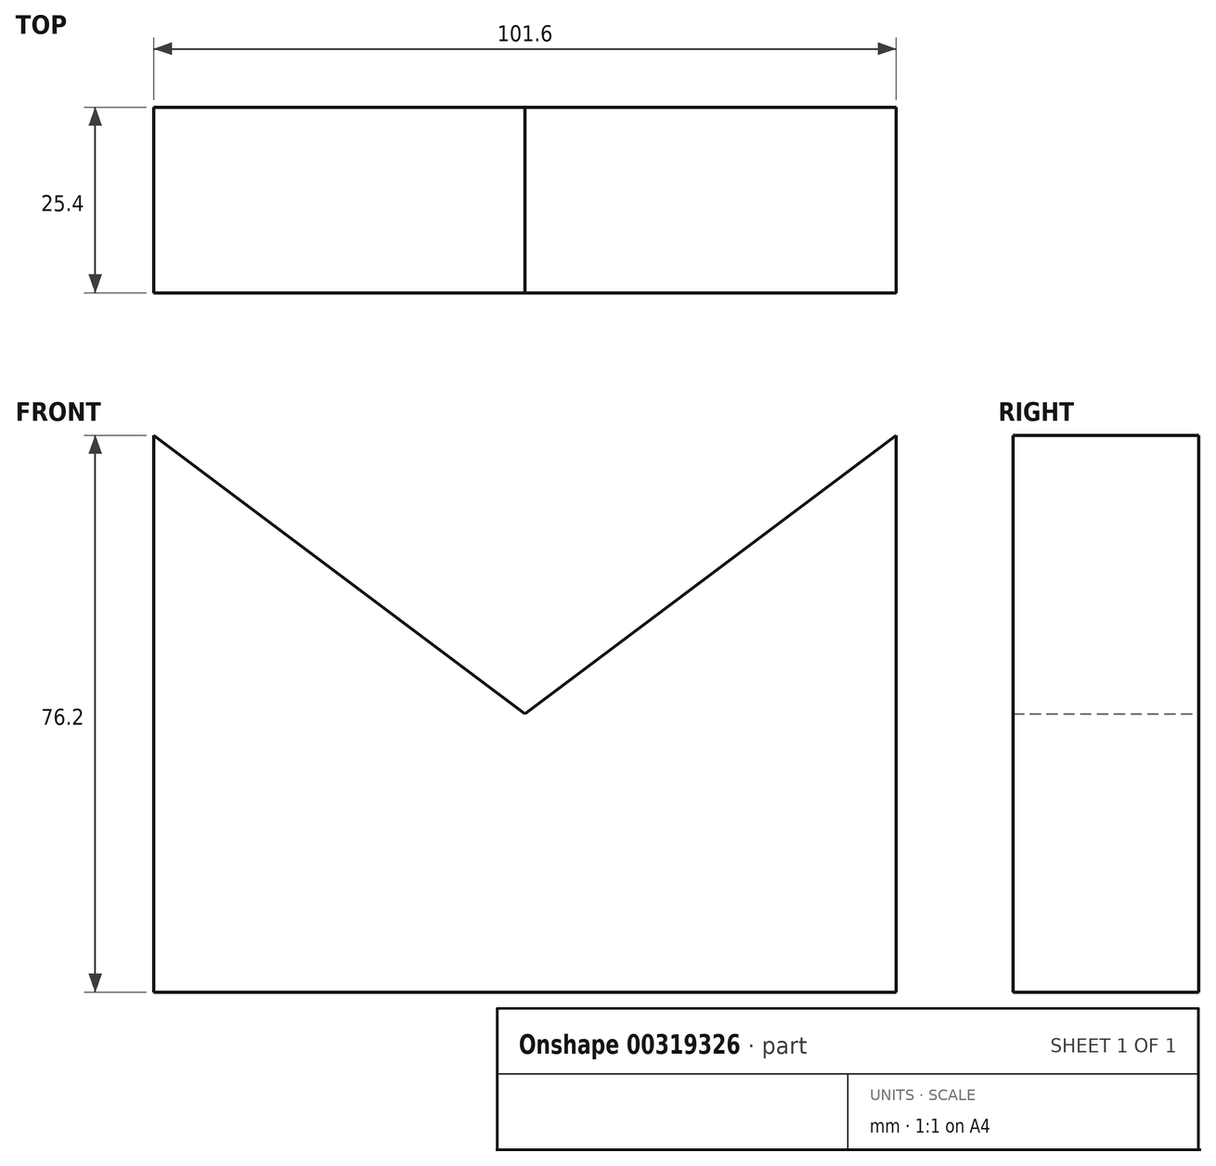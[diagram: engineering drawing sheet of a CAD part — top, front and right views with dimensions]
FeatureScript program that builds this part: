
annotation { "Feature Type Name" : "Feature", "Feature Type Description" : "" }
export const myFeature = defineFeature(function(context is Context, id is Id, definition is map)
    precondition{}
    {
        {
            var Q0;
            Q0=qCreatedBy(makeId("Front.planeOp"),FACE);
            var sketch = newSketch(context, id + "F0", { "sketchPlane" : qUnion([Q0])});
            skLineSegment(sketch, "E0", {"start": v(-44, -55.57) * mm, "end": v(57.6, -55.57) * mm});
            skLineSegment(sketch, "E1", {"start": v(57.6, -55.57) * mm, "end": v(57.6, 20.63) * mm});
            skLineSegment(sketch, "E2", {"start": v(-44, 20.63) * mm, "end": v(-44, -55.57) * mm});
            skLineSegment(sketch, "E3", {"start": v(6.8, -17.47) * mm, "end": v(57.6, 20.63) * mm});
            skPoint(sketch, "E3.startSnap0", {"position": v(6.8, -55.57) * mm});
            skLineSegment(sketch, "E4", {"start": v(-44, 20.63) * mm, "end": v(6.8, -17.47) * mm});
            skSolve(sketch);
        }
        {
            var Q0;
            Q0 = qSketchRegion(id + "F0", true);
            var Q1;
            Q1=makeQuery(id+"F0.imprint","IMPRINT",FACE,{"disambiguationData":[TD([[makeQuery(id+"F0.imprint","IMPRINT",EDGE,{"derivedFrom":sQuery(id+"F0.wireOp",EDGE,"E0")}),1.0]])]});
            extrude(context, id + "F1", {"entities" : qUnion([Q0, Q1]), "depth" : 25.4 * mm});
        }
    });
